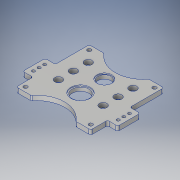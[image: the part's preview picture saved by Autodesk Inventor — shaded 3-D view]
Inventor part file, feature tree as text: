
AUTODESK INVENTOR PART (.ipt)
format: ipt  version: 2019 (Build 230136000, 136)  size: 291,840 bytes
history: native  units: in
note: dims shown in document units (in); Inventor stores cm internally (conversion verified against a paired STEP export)
features: extrude x6, sketch x6, fillet x3
ambient origin geometry x8: Origin, YZ Plane, XZ Plane, XY Plane, X Axis, Y Axis, Z Axis, Center Point
bodies: Solid1 (feature_tree)
feature tree (15):
  extrude  "Extrusion1"  Depth=4.9in
  extrude  "Extrusion2"  Depth=0.3125in
  fillet  "Fillet1"  Radius=0.312in
  extrude  "Extrusion6"  Depth=0.312in
  extrude  "Extrusion7"  Depth=0.256in
  fillet  "Fillet3"  Radius=1.0in
  extrude  "Extrusion8"  Depth=0.5in
  fillet  "Fillet4"  Radius=0.5in
  extrude  "Extrusion9"  Depth=1.125in
  sketch  "Sketch1"  dims[d0=5.0in d1=4.9in]
  sketch  "Sketch2"  dims[d2=0.3125in d3=0.0in d4=0.312in d5=0.312in]
  sketch  "Sketch6"  dims[d6=0.312in d7=0.312in]
  sketch  "Sketch7"  dims[d8=0.256in d9=0.256in d10=1.0in]
  sketch  "Sketch8"  dims[d11=1.067in d12=1.0in d14=0.5in]
  sketch  "Sketch12"  dims[d15=1.0in d17=1.125in d18=1.602in d19=0.3125in d20=0.0in d21=0.125in d47=0.125in d48=1.5in d49=0.688in d50=0.688in d51=0.3125in d52=0.0in d53=0.375in d54=0.375in d55=0.2in d56=0.344in d57=0.3125in d58=0.0in d59=0.125in d60=0.75in d61=1.5in d62=3.0in d63=0.75in d64=0.3125in d65=0.0in d66=1.067in d67=0.125in d69=1.5in d70=0.375in d71=0.375in d72=0.375in d75=1.0in d76=1.485in d77=1.5in d78=1.5in d79=0.125in d80=1.0in d81=1.0in d82=1.125in d83=1.125in d84=1.0in d97=1.3in d98=1.0in d99=0.0625in d100=0.0in]
